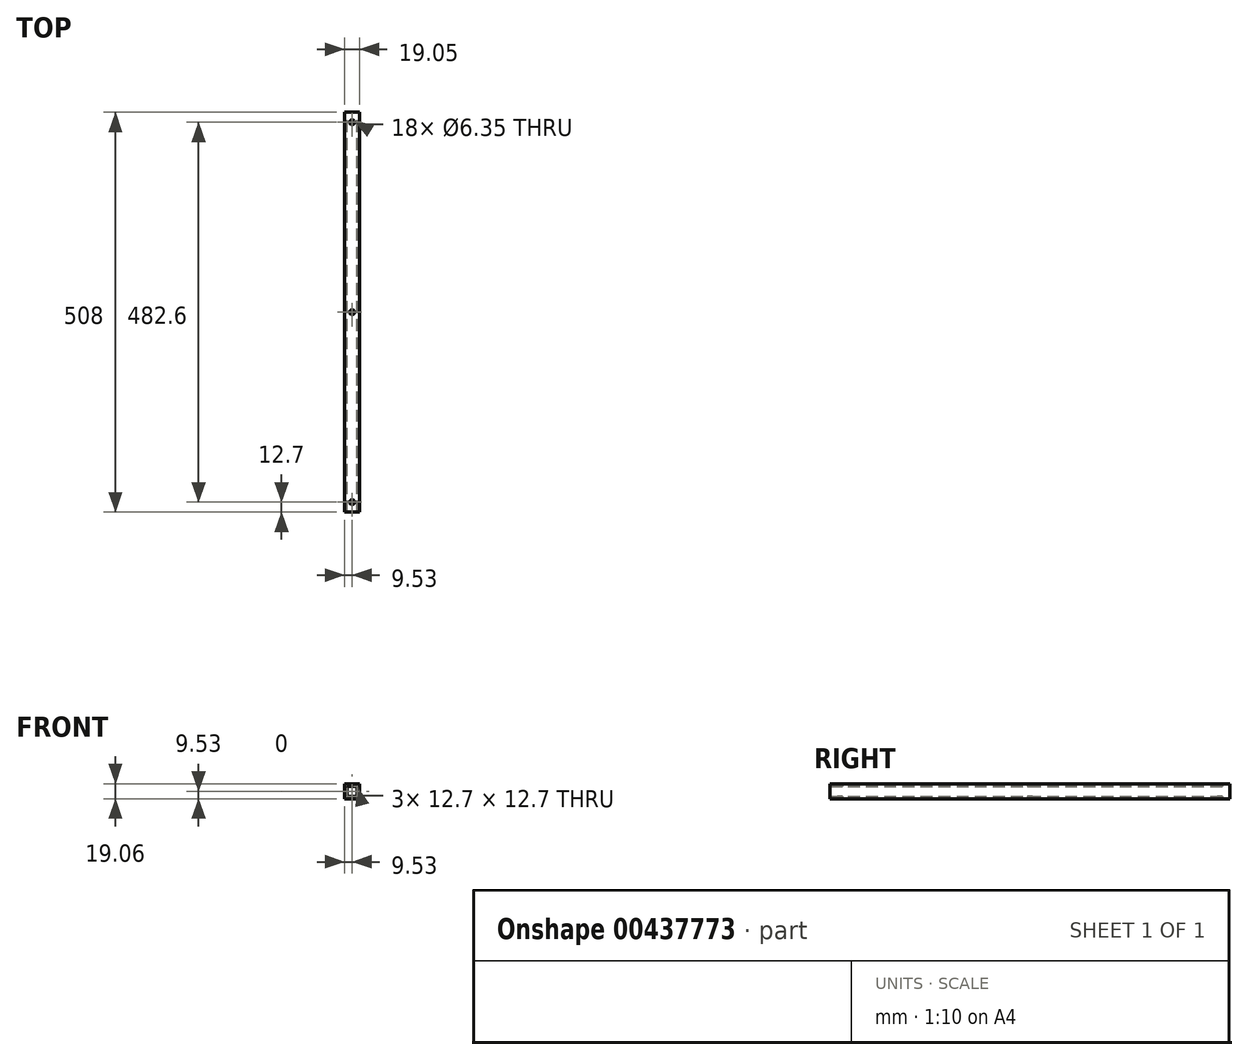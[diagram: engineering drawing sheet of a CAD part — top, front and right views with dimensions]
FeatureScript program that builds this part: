
annotation { "Feature Type Name" : "Feature", "Feature Type Description" : "" }
export const myFeature = defineFeature(function(context is Context, id is Id, definition is map)
    precondition{}
    {
        {
            var Q0;
            Q0=qCreatedBy(makeId("Front.planeOp"),FACE);
            var sketch = newSketch(context, id + "F0", { "sketchPlane" : qUnion([Q0])});
            skLineSegment(sketch, "E0.bottom", {"start": v(-15.88, 15.88) * mm, "end": v(3.17, 15.88) * mm});
            skLineSegment(sketch, "E0.top", {"start": v(-15.88, -3.18) * mm, "end": v(3.18, -3.18) * mm});
            skLineSegment(sketch, "E0.left", {"start": v(-15.88, 15.88) * mm, "end": v(-15.88, -3.18) * mm});
            skLineSegment(sketch, "E0.right", {"start": v(3.17, 15.88) * mm, "end": v(3.18, -3.18) * mm});
            skLineSegment(sketch, "E1.bottom", {"start": v(-12.7, 12.7) * mm, "end": v(0, 12.7) * mm});
            skLineSegment(sketch, "E1.top", {"start": v(-12.7, 0) * mm, "end": v(0, 0) * mm});
            skLineSegment(sketch, "E1.left", {"start": v(-12.7, 12.7) * mm, "end": v(-12.7, 0) * mm});
            skLineSegment(sketch, "E1.right", {"start": v(0, 12.7) * mm, "end": v(0, 0) * mm});
            skSolve(sketch);
        }
        {
            var Q0;
            Q0=qSketchRegion(id+"F0",true);
            extrude(context, id + "F1", {"entities" : qUnion([Q0]), "depth" : 508 * mm});
        }
        {
            var Q0;
            Q0=qCreatedBy(makeId("Top.planeOp"),FACE);
            var sketch = newSketch(context, id + "F2", { "sketchPlane" : qUnion([Q0])});
            skCircle(sketch, "E2", {"center": v(-6.35, -12.7) * mm, "radius": 3.17 * mm});
            skCircle(sketch, "E3", {"center": v(-6.35, -254) * mm, "radius": 3.17 * mm});
            skCircle(sketch, "E4", {"center": v(-6.35, -495.3) * mm, "radius": 3.17 * mm});
            skSolve(sketch);
        }
        {
            var Q0;
            Q0 = qSketchRegion(id + "F2", true);
            extrude(context, id + "F3", {"entities" : qUnion([Q0]), "operationType" : NewBodyOperationType.REMOVE, "depth" : 127 * mm, "symmetric" : true});
        }
    });
